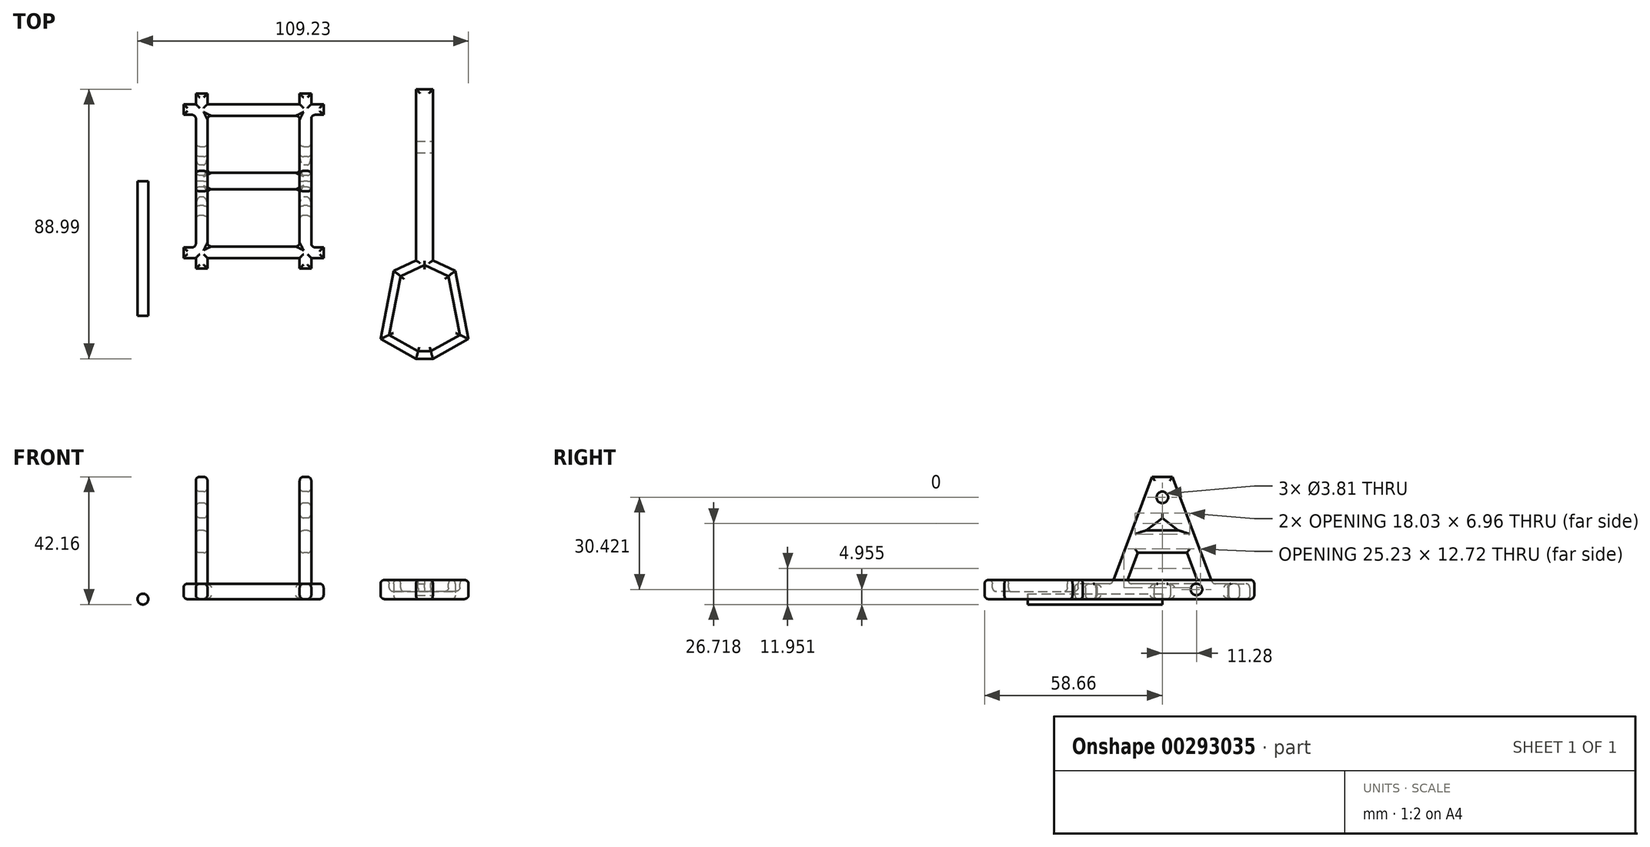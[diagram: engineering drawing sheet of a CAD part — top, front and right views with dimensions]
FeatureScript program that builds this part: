
annotation { "Feature Type Name" : "Feature", "Feature Type Description" : "" }
export const myFeature = defineFeature(function(context is Context, id is Id, definition is map)
    precondition{}
    {
        {
            var Q0;
            Q0=qCreatedBy(makeId("Top.planeOp"),FACE);
            var sketch = newSketch(context, id + "F0", { "sketchPlane" : qUnion([Q0])});
            skLineSegment(sketch, "E0.bottom", {"start": v(19.05, 25.4) * mm, "end": v(-19.05, 25.4) * mm});
            skLineSegment(sketch, "E0.top", {"start": v(19.05, -25.4) * mm, "end": v(-19.05, -25.4) * mm});
            skLineSegment(sketch, "E0.left", {"start": v(19.05, 21.89) * mm, "end": v(19.05, -21.89) * mm});
            skLineSegment(sketch, "E0.right", {"start": v(-19.05, 21.89) * mm, "end": v(-19.05, -21.89) * mm});
            skPoint(sketch, "E0.middle", {"position": v(0, 0) * mm});
            skLineSegment(sketch, "E1", {"start": v(-19.05, 25.4) * mm, "end": v(-23.1, 25.4) * mm});
            skLineSegment(sketch, "E2", {"start": v(-23.1, 25.4) * mm, "end": v(-23.1, 21.89) * mm});
            skLineSegment(sketch, "E3", {"start": v(-23.1, 21.89) * mm, "end": v(-19.05, 21.89) * mm});
            skLineSegment(sketch, "E4.MirrorCS", {"start": v(-23.1, -25.4) * mm, "end": v(-23.1, -21.89) * mm});
            skLineSegment(sketch, "E5.MirrorCS", {"start": v(-19.05, -25.4) * mm, "end": v(-23.1, -25.4) * mm});
            skLineSegment(sketch, "E6.MirrorCS", {"start": v(-23.1, -21.89) * mm, "end": v(-19.05, -21.89) * mm});
            skLineSegment(sketch, "E7.MirrorCS", {"start": v(23.1, 21.89) * mm, "end": v(19.05, 21.89) * mm});
            skLineSegment(sketch, "E8.MirrorCS", {"start": v(23.1, 25.4) * mm, "end": v(23.1, 21.89) * mm});
            skLineSegment(sketch, "E9.MirrorCS", {"start": v(19.05, 25.4) * mm, "end": v(23.1, 25.4) * mm});
            skLineSegment(sketch, "E10.MirrorCS", {"start": v(23.1, -21.89) * mm, "end": v(19.05, -21.89) * mm});
            skLineSegment(sketch, "E11.MirrorCS", {"start": v(23.1, -25.4) * mm, "end": v(23.1, -21.89) * mm});
            skLineSegment(sketch, "E12.MirrorCS", {"start": v(19.05, -25.4) * mm, "end": v(23.1, -25.4) * mm});
            skLineSegment(sketch, "E13.bottom", {"start": v(-15.23, 21.58) * mm, "end": v(15.23, 21.58) * mm});
            skLineSegment(sketch, "E13.top", {"start": v(-15.23, -21.58) * mm, "end": v(15.23, -21.58) * mm});
            skLineSegment(sketch, "E13.left", {"start": v(-15.23, 21.58) * mm, "end": v(-15.23, 2.71) * mm});
            skLineSegment(sketch, "E13.right", {"start": v(15.23, 21.58) * mm, "end": v(15.23, 2.71) * mm});
            skLineSegment(sketch, "E14", {"start": v(-15.23, 2.71) * mm, "end": v(15.23, 2.71) * mm});
            skPoint(sketch, "E15.endSnap0", {"position": v(-15.23, 0) * mm});
            skLineSegment(sketch, "E16.MirrorCS", {"start": v(-15.23, -2.71) * mm, "end": v(15.23, -2.71) * mm});
            skLineSegment(sketch, "E17.trimOffspring", {"start": v(-15.23, -2.71) * mm, "end": v(-15.23, -21.58) * mm});
            skLineSegment(sketch, "E18.trimOffspring", {"start": v(15.23, -2.71) * mm, "end": v(15.23, -21.58) * mm});
            skLineSegment(sketch, "E19", {"start": v(-19.05, -25.4) * mm, "end": v(-19.05, -28.88) * mm});
            skLineSegment(sketch, "E20", {"start": v(-19.05, -28.88) * mm, "end": v(-15.23, -28.88) * mm});
            skLineSegment(sketch, "E21", {"start": v(-15.23, -28.88) * mm, "end": v(-15.23, -25.4) * mm});
            skPoint(sketch, "E22.endSnap0", {"position": v(0, -2.71) * mm});
            skLineSegment(sketch, "E23.MirrorCS", {"start": v(19.05, -28.88) * mm, "end": v(15.23, -28.88) * mm});
            skLineSegment(sketch, "E24.MirrorCS", {"start": v(19.05, -25.4) * mm, "end": v(19.05, -28.88) * mm});
            skLineSegment(sketch, "E25.MirrorCS", {"start": v(15.23, -28.88) * mm, "end": v(15.23, -25.4) * mm});
            skLineSegment(sketch, "E26.MirrorCS", {"start": v(-19.05, 25.4) * mm, "end": v(-19.05, 28.88) * mm});
            skLineSegment(sketch, "E27.MirrorCS", {"start": v(-19.05, 28.88) * mm, "end": v(-15.23, 28.88) * mm});
            skLineSegment(sketch, "E28.MirrorCS", {"start": v(-15.23, 28.88) * mm, "end": v(-15.23, 25.4) * mm});
            skLineSegment(sketch, "E29.MirrorCS", {"start": v(15.23, 28.88) * mm, "end": v(15.23, 25.4) * mm});
            skLineSegment(sketch, "E30.MirrorCS", {"start": v(19.05, 28.88) * mm, "end": v(15.23, 28.88) * mm});
            skLineSegment(sketch, "E31.MirrorCS", {"start": v(19.05, 25.4) * mm, "end": v(19.05, 28.88) * mm});
            skPoint(sketch, "E32.orphan", {"position": v(0, -8.45) * mm});
            skSolve(sketch);
        }
        {
            var Q0;
            Q0 = qSketchRegion(id + "F0", true);
            extrude(context, id + "F1", {"entities" : qUnion([Q0]), "depth" : 5.08 * mm});
        }
        {
            var Q0;
            Q0=qCreatedBy(makeId("Right.planeOp"),FACE);
            var sketch = newSketch(context, id + "F2", { "sketchPlane" : qUnion([Q0])});
            skLineSegment(sketch, "E33.0.0", {"start": v(21.89, 0) * mm, "end": v(-21.89, 0) * mm});
            skLineSegment(sketch, "E33.0.1", {"start": v(-21.89, 0) * mm, "end": v(-21.89, 5.08) * mm});
            skLineSegment(sketch, "E33.0.2", {"start": v(-21.89, 5.08) * mm, "end": v(21.89, 5.08) * mm});
            skLineSegment(sketch, "E33.0.3", {"start": v(21.89, 5.08) * mm, "end": v(21.89, 0) * mm});
            skLineSegment(sketch, "E34", {"start": v(16.63, 5.08) * mm, "end": v(3.36, 40.38) * mm});
            skLineSegment(sketch, "E35.MirrorCS", {"start": v(-16.63, 5.08) * mm, "end": v(-3.36, 40.38) * mm});
            skLineSegment(sketch, "E36", {"start": v(3.36, 40.38) * mm, "end": v(-3.36, 40.38) * mm});
            skLineSegment(sketch, "E37", {"start": v(11.93, 5.08) * mm, "end": v(8.1, 15.26) * mm});
            skLineSegment(sketch, "E38", {"start": v(0, 0) * mm, "end": v(0, 15.33) * mm});
            skLineSegment(sketch, "E39.MirrorCS", {"start": v(-11.93, 5.08) * mm, "end": v(-8.1, 15.26) * mm});
            skPoint(sketch, "E40.orphan", {"position": v(-0.73, 38.74) * mm});
            skPoint(sketch, "E41.orphan", {"position": v(0.73, 38.74) * mm});
            skLineSegment(sketch, "E42", {"start": v(5.29, 22.73) * mm, "end": v(-5.29, 22.73) * mm});
            skLineSegment(sketch, "E43", {"start": v(8.1, 15.26) * mm, "end": v(-8.1, 15.26) * mm});
            skPoint(sketch, "E44.orphan", {"position": v(-10, 22.73) * mm});
            skPoint(sketch, "E45.orphan", {"position": v(10, 22.73) * mm});
            skLineSegment(sketch, "E46", {"start": v(5.29, 22.73) * mm, "end": v(0, 26.81) * mm});
            skLineSegment(sketch, "E47", {"start": v(0, 26.81) * mm, "end": v(-5.29, 22.73) * mm});
            skLineSegment(sketch, "E48", {"start": v(0, 40.38) * mm, "end": v(0, 26.81) * mm});
            skCircle(sketch, "E49", {"center": v(0, 33.6) * mm, "radius": 1.9 * mm});
            skSolve(sketch);
        }
        {
            var Q0;
            {var subQ6=sQuery(id+"F2.wireOp",EDGE,"E34");Q0=makeQuery(id+"F2.imprint","IMPRINT",FACE,{"disambiguationData":[TD([[makeQuery(id+"F2.imprint","IMPRINT",EDGE,{"derivedFrom":subQ6}),1.0]])]});}
            extrude(context, id + "F3", {"entities" : qUnion([Q0]), "operationType" : NewBodyOperationType.ADD, "depth" : 19.05 * mm, "hasSecondDirection" : true, "secondDirectionOppositeDirection" : true, "secondDirectionDepth" : 19.05 * mm});
        }
        {
            var Q0;
            Q0=makeQuery(id+"F3.opExtrude","SWEPT_FACE",FACE,{"disambiguationData":[OSD([sQuery(id+"F2.wireOp",EDGE,"E36")])]});
            var sketch = newSketch(context, id + "F4", { "sketchPlane" : qUnion([Q0])});
            skLineSegment(sketch, "E50.0.0", {"start": v(-19.05, 16.63) * mm, "end": v(-19.05, 3.36) * mm});
            skLineSegment(sketch, "E50.0.1", {"start": v(-19.05, 3.36) * mm, "end": v(19.05, 3.36) * mm});
            skLineSegment(sketch, "E50.0.2", {"start": v(19.05, 3.36) * mm, "end": v(19.05, 16.63) * mm});
            skLineSegment(sketch, "E50.0.3", {"start": v(19.05, 16.63) * mm, "end": v(15.23, 16.63) * mm});
            skLineSegment(sketch, "E50.0.4", {"start": v(15.23, 16.63) * mm, "end": v(-15.23, 16.63) * mm});
            skLineSegment(sketch, "E50.0.5", {"start": v(-15.23, 16.63) * mm, "end": v(-19.05, 16.63) * mm});
            skLineSegment(sketch, "E51.0.0", {"start": v(-19.05, -3.36) * mm, "end": v(-19.05, -16.63) * mm});
            skLineSegment(sketch, "E51.0.1", {"start": v(-19.05, -16.63) * mm, "end": v(-15.23, -16.63) * mm});
            skLineSegment(sketch, "E51.0.2", {"start": v(-15.23, -16.63) * mm, "end": v(15.23, -16.63) * mm});
            skLineSegment(sketch, "E51.0.3", {"start": v(15.23, -16.63) * mm, "end": v(19.05, -16.63) * mm});
            skLineSegment(sketch, "E51.0.4", {"start": v(19.05, -16.63) * mm, "end": v(19.05, -3.36) * mm});
            skLineSegment(sketch, "E51.0.5", {"start": v(19.05, -3.36) * mm, "end": v(-19.05, -3.36) * mm});
            skLineSegment(sketch, "E52.0.0", {"start": v(19.05, -21.89) * mm, "end": v(19.05, -16.63) * mm});
            skLineSegment(sketch, "E52.0.1", {"start": v(19.05, -16.63) * mm, "end": v(15.23, -16.63) * mm});
            skLineSegment(sketch, "E52.0.2", {"start": v(15.23, -16.63) * mm, "end": v(15.23, -21.58) * mm});
            skLineSegment(sketch, "E52.0.3", {"start": v(15.23, -21.58) * mm, "end": v(-15.23, -21.58) * mm});
            skLineSegment(sketch, "E52.0.4", {"start": v(-15.23, -21.58) * mm, "end": v(-15.23, -16.63) * mm});
            skLineSegment(sketch, "E52.0.5", {"start": v(-15.23, -16.63) * mm, "end": v(-19.05, -16.63) * mm});
            skLineSegment(sketch, "E52.0.6", {"start": v(-19.05, -16.63) * mm, "end": v(-19.05, -21.89) * mm});
            skLineSegment(sketch, "E52.0.7", {"start": v(-19.05, -21.89) * mm, "end": v(-23.1, -21.89) * mm});
            skLineSegment(sketch, "E52.0.8", {"start": v(-23.1, -21.89) * mm, "end": v(-23.1, -25.4) * mm});
            skLineSegment(sketch, "E52.0.9", {"start": v(-23.1, -25.4) * mm, "end": v(-19.05, -25.4) * mm});
            skLineSegment(sketch, "E52.0.10", {"start": v(-19.05, -25.4) * mm, "end": v(-19.05, -28.88) * mm});
            skLineSegment(sketch, "E52.0.11", {"start": v(-19.05, -28.88) * mm, "end": v(-15.23, -28.88) * mm});
            skLineSegment(sketch, "E52.0.12", {"start": v(-15.23, -28.88) * mm, "end": v(-15.23, -25.4) * mm});
            skLineSegment(sketch, "E52.0.13", {"start": v(-15.23, -25.4) * mm, "end": v(15.23, -25.4) * mm});
            skLineSegment(sketch, "E52.0.14", {"start": v(15.23, -25.4) * mm, "end": v(15.23, -28.88) * mm});
            skLineSegment(sketch, "E52.0.15", {"start": v(15.23, -28.88) * mm, "end": v(19.05, -28.88) * mm});
            skLineSegment(sketch, "E52.0.16", {"start": v(19.05, -28.88) * mm, "end": v(19.05, -25.4) * mm});
            skLineSegment(sketch, "E52.0.17", {"start": v(19.05, -25.4) * mm, "end": v(23.1, -25.4) * mm});
            skLineSegment(sketch, "E52.0.18", {"start": v(23.1, -25.4) * mm, "end": v(23.1, -21.89) * mm});
            skLineSegment(sketch, "E52.0.19", {"start": v(23.1, -21.89) * mm, "end": v(19.05, -21.89) * mm});
            skLineSegment(sketch, "E53", {"start": v(-15.23, -16.63) * mm, "end": v(-15.23, 16.63) * mm});
            skLineSegment(sketch, "E54", {"start": v(15.23, 16.63) * mm, "end": v(15.23, -16.63) * mm});
            skSolve(sketch);
        }
        {
            var Q0;
            {var subQ5=sQuery(id+"F4.wireOp",EDGE,"E50.0.4");Q0=makeQuery(id+"F4.imprint","IMPRINT",FACE,{"disambiguationData":[TD([[makeQuery(id+"F4.imprint","IMPRINT",EDGE,{"derivedFrom":subQ5}),1.0]])]});}
            var Q1;
            {var subQ0=sQuery(id+"F4.wireOp",EDGE,"E54");var subQ1=sQuery(id+"F4.wireOp",EDGE,"E50.0.1");var subQ2=makeQuery(id+"F4.imprint","INTERSECT",VERTEX,{"derivedFrom":[subQ1,subQ0]});Q1=makeQuery(id+"F4.imprint","IMPRINT",FACE,{"disambiguationData":[TD([[makeQuery(id+"F4.imprint","IMPRINT",EDGE,{"disambiguationData":[TD([[subQ2,-1.0]])],"derivedFrom":subQ1}),1.0]])]});}
            var Q2;
            {var subQ0=sQuery(id+"F4.wireOp",EDGE,"E51.0.2");Q2=makeQuery(id+"F4.imprint","IMPRINT",FACE,{"disambiguationData":[TD([[makeQuery(id+"F4.imprint","IMPRINT",EDGE,{"derivedFrom":subQ0}),1.0]])]});}
            var Q3;
            {var subQ0=sQuery(id+"F0.wireOp",EDGE,"E18.trimOffspring");var subQ11=sQuery(id+"F0.wireOp",EDGE,"E0.right");var subQ12=sQuery(id+"F0.wireOp",EDGE,"E17.trimOffspring");var subQ13=sQuery(id+"F0.wireOp",EDGE,"E0.left");var subQ14=sQuery(id+"F0.wireOp",EDGE,"E16.MirrorCS");var subQ15=sQuery(id+"F0.wireOp",EDGE,"E14");var subQ16=sQuery(id+"F0.wireOp",EDGE,"E13.left");var subQ17=sQuery(id+"F0.wireOp",EDGE,"E13.right");Q3=makeQuery(id+"F3.boolean.opBoolean","SPLIT",FACE,{"disambiguationData":[TD([makeQuery(id+"F1.opExtrude","SWEPT_FACE",FACE,{"disambiguationData":[OSD([subQ15])]})])],"derivedFrom":makeQuery(id+"F1.opExtrude","CAP_FACE",FACE,{"disambiguationData":[OSD([sQuery(id+"F0.wireOp",EDGE,"E0.bottom"),sQuery(id+"F0.wireOp",EDGE,"E0.top"),subQ13,subQ11,sQuery(id+"F0.wireOp",EDGE,"E1"),sQuery(id+"F0.wireOp",EDGE,"E2"),sQuery(id+"F0.wireOp",EDGE,"E3"),sQuery(id+"F0.wireOp",EDGE,"E4.MirrorCS"),sQuery(id+"F0.wireOp",EDGE,"E5.MirrorCS"),sQuery(id+"F0.wireOp",EDGE,"E6.MirrorCS"),sQuery(id+"F0.wireOp",EDGE,"E7.MirrorCS"),sQuery(id+"F0.wireOp",EDGE,"E8.MirrorCS"),sQuery(id+"F0.wireOp",EDGE,"E9.MirrorCS"),sQuery(id+"F0.wireOp",EDGE,"E10.MirrorCS"),sQuery(id+"F0.wireOp",EDGE,"E11.MirrorCS"),sQuery(id+"F0.wireOp",EDGE,"E12.MirrorCS"),sQuery(id+"F0.wireOp",EDGE,"E13.bottom"),sQuery(id+"F0.wireOp",EDGE,"E13.top"),subQ16,subQ17,subQ15,subQ14,subQ12,subQ0,sQuery(id+"F0.wireOp",EDGE,"E19"),sQuery(id+"F0.wireOp",EDGE,"E20"),sQuery(id+"F0.wireOp",EDGE,"E21"),sQuery(id+"F0.wireOp",EDGE,"E23.MirrorCS"),sQuery(id+"F0.wireOp",EDGE,"E24.MirrorCS"),sQuery(id+"F0.wireOp",EDGE,"E25.MirrorCS"),sQuery(id+"F0.wireOp",EDGE,"E26.MirrorCS"),sQuery(id+"F0.wireOp",EDGE,"E27.MirrorCS"),sQuery(id+"F0.wireOp",EDGE,"E28.MirrorCS"),sQuery(id+"F0.wireOp",EDGE,"E29.MirrorCS"),sQuery(id+"F0.wireOp",EDGE,"E30.MirrorCS"),sQuery(id+"F0.wireOp",EDGE,"E31.MirrorCS")])],"isStart":false})});}
            extrude(context, id + "F5", {"entities" : qUnion([Q0, Q1, Q2]), "operationType" : NewBodyOperationType.REMOVE, "endBound" : BoundingType.UP_TO_SURFACE, "oppositeDirection" : true, "endBoundEntityFace" : qUnion([Q3]), "depth" : 25.4 * mm});
        }
        {
            var Q0;
            Q0=qCreatedBy(makeId("Top.planeOp"),FACE);
            var sketch = newSketch(context, id + "F6", { "sketchPlane" : qUnion([Q0])});
            skLineSegment(sketch, "E55", {"start": v(59.18, 0) * mm, "end": v(59.18, 30.33) * mm});
            skLineSegment(sketch, "E56", {"start": v(59.18, 30.33) * mm, "end": v(53.67, 30.33) * mm});
            skLineSegment(sketch, "E57", {"start": v(53.67, 30.33) * mm, "end": v(53.67, -26.25) * mm});
            skLineSegment(sketch, "E58", {"start": v(53.67, -26.25) * mm, "end": v(46.26, -29.62) * mm});
            skLineSegment(sketch, "E59", {"start": v(46.26, -29.62) * mm, "end": v(41.91, -52.14) * mm});
            skLineSegment(sketch, "E60", {"start": v(41.91, -52.14) * mm, "end": v(53.67, -58.66) * mm});
            skLineSegment(sketch, "E61", {"start": v(53.67, -58.66) * mm, "end": v(56.42, -58.66) * mm});
            skPoint(sketch, "E61.endSnap0", {"position": v(56.42, 30.33) * mm});
            skLineSegment(sketch, "E62", {"start": v(56.42, -58.66) * mm, "end": v(56.42, -51.22) * mm});
            skLineSegment(sketch, "E63.MirrorCS", {"start": v(59.18, -58.66) * mm, "end": v(56.42, -58.66) * mm});
            skLineSegment(sketch, "E64.MirrorCS", {"start": v(70.94, -52.14) * mm, "end": v(59.18, -58.66) * mm});
            skLineSegment(sketch, "E65.MirrorCS", {"start": v(66.6, -29.62) * mm, "end": v(70.94, -52.14) * mm});
            skLineSegment(sketch, "E66.MirrorCS", {"start": v(59.18, -26.25) * mm, "end": v(66.6, -29.62) * mm});
            skLineSegment(sketch, "E67.MirrorCS", {"start": v(59.18, 30.33) * mm, "end": v(59.18, -26.25) * mm});
            skSolve(sketch);
        }
        {
            var Q0;
            Q0 = qSketchRegion(id + "F6", true);
            extrude(context, id + "F7", {"entities" : qUnion([Q0]), "depth" : 6.35 * mm});
        }
        {
            var Q0;
            Q0=makeQuery(id+"F7.opExtrude","CAP_FACE",FACE,{"disambiguationData":[OSD([sQuery(id+"F6.wireOp",EDGE,"E56"),sQuery(id+"F6.wireOp",EDGE,"E57"),sQuery(id+"F6.wireOp",EDGE,"E58"),sQuery(id+"F6.wireOp",EDGE,"E59"),sQuery(id+"F6.wireOp",EDGE,"E60"),sQuery(id+"F6.wireOp",EDGE,"E61"),sQuery(id+"F6.wireOp",EDGE,"E63.MirrorCS"),sQuery(id+"F6.wireOp",EDGE,"E64.MirrorCS"),sQuery(id+"F6.wireOp",EDGE,"E65.MirrorCS"),sQuery(id+"F6.wireOp",EDGE,"E66.MirrorCS"),sQuery(id+"F6.wireOp",EDGE,"E67.MirrorCS")])],"isStart":false});
            var sketch = newSketch(context, id + "F8", { "sketchPlane" : qUnion([Q0])});
            skLineSegment(sketch, "E68.0", {"start": v(44.75, -50.8) * mm, "end": v(54.33, -56.12) * mm});
            skLineSegment(sketch, "E68.1", {"start": v(48.5, -31.4) * mm, "end": v(44.75, -50.8) * mm});
            skLineSegment(sketch, "E68.2", {"start": v(58.52, -56.12) * mm, "end": v(68.1, -50.8) * mm});
            skLineSegment(sketch, "E68.3", {"start": v(68.1, -50.8) * mm, "end": v(64.35, -31.4) * mm});
            skLineSegment(sketch, "E68.4", {"start": v(64.35, -31.4) * mm, "end": v(56.42, -27.78) * mm});
            skLineSegment(sketch, "E68.5", {"start": v(54.33, -56.12) * mm, "end": v(58.52, -56.12) * mm});
            skLineSegment(sketch, "E68.6", {"start": v(56.42, -27.78) * mm, "end": v(48.5, -31.4) * mm});
            skSolve(sketch);
        }
        {
            var Q0;
            Q0 = qSketchRegion(id + "F8", true);
            extrude(context, id + "F9", {"entities" : qUnion([Q0]), "operationType" : NewBodyOperationType.REMOVE, "oppositeDirection" : true, "depth" : 3.8 * mm});
        }
        {
            var Q0;
            Q0=makeQuery(id+"F7.opExtrude","SWEPT_FACE",FACE,{"disambiguationData":[OSD([sQuery(id+"F6.wireOp",EDGE,"E67.MirrorCS")])]});
            var sketch = newSketch(context, id + "F10", { "sketchPlane" : qUnion([Q0])});
            skLineSegment(sketch, "E69", {"start": v(30.33, 3.18) * mm, "end": v(11.28, 3.18) * mm});
            skCircle(sketch, "E70", {"center": v(11.28, 3.18) * mm, "radius": 1.9 * mm});
            skSolve(sketch);
        }
        {
            var Q0;
            Q0 = qSketchRegion(id + "F10", true);
            extrude(context, id + "F11", {"entities" : qUnion([Q0]), "operationType" : NewBodyOperationType.REMOVE, "oppositeDirection" : true, "depth" : 25.4 * mm});
        }
        {
            var Q0;
            Q0=makeQuery(id+"F9.boolean.opBoolean","COPY",FACE,{"derivedFrom":makeQuery(id+"F9.opExtrude","CAP_FACE",FACE,{"disambiguationData":[OSD([sQuery(id+"F8.wireOp",EDGE,"E68.0"),sQuery(id+"F8.wireOp",EDGE,"E68.1"),sQuery(id+"F8.wireOp",EDGE,"E68.2"),sQuery(id+"F8.wireOp",EDGE,"E68.3"),sQuery(id+"F8.wireOp",EDGE,"E68.4"),sQuery(id+"F8.wireOp",EDGE,"E68.5"),sQuery(id+"F8.wireOp",EDGE,"E68.6")])],"isStart":false})});
            var Q1;
            Q1=makeQuery(id+"F9.boolean.opBoolean","COPY",EDGE,{"derivedFrom":makeQuery(id+"F9.opExtrude","CAP_EDGE",EDGE,{"disambiguationData":[OSD([sQuery(id+"F8.wireOp",EDGE,"E68.0")])],"isStart":true})});
            var Q2;
            Q2=makeQuery(id+"F7.opExtrude","CAP_FACE",FACE,{"disambiguationData":[OSD([sQuery(id+"F6.wireOp",EDGE,"E56"),sQuery(id+"F6.wireOp",EDGE,"E57"),sQuery(id+"F6.wireOp",EDGE,"E58"),sQuery(id+"F6.wireOp",EDGE,"E59"),sQuery(id+"F6.wireOp",EDGE,"E60"),sQuery(id+"F6.wireOp",EDGE,"E61"),sQuery(id+"F6.wireOp",EDGE,"E63.MirrorCS"),sQuery(id+"F6.wireOp",EDGE,"E64.MirrorCS"),sQuery(id+"F6.wireOp",EDGE,"E65.MirrorCS"),sQuery(id+"F6.wireOp",EDGE,"E66.MirrorCS"),sQuery(id+"F6.wireOp",EDGE,"E67.MirrorCS")])],"isStart":false});
            var Q3;
            Q3=makeQuery(id+"F7.opExtrude","CAP_FACE",FACE,{"disambiguationData":[OSD([sQuery(id+"F6.wireOp",EDGE,"E56"),sQuery(id+"F6.wireOp",EDGE,"E57"),sQuery(id+"F6.wireOp",EDGE,"E58"),sQuery(id+"F6.wireOp",EDGE,"E59"),sQuery(id+"F6.wireOp",EDGE,"E60"),sQuery(id+"F6.wireOp",EDGE,"E61"),sQuery(id+"F6.wireOp",EDGE,"E63.MirrorCS"),sQuery(id+"F6.wireOp",EDGE,"E64.MirrorCS"),sQuery(id+"F6.wireOp",EDGE,"E65.MirrorCS"),sQuery(id+"F6.wireOp",EDGE,"E66.MirrorCS"),sQuery(id+"F6.wireOp",EDGE,"E67.MirrorCS")])],"isStart":true});
            fillet(context, id + "F12", {"entities" : qUnion([Q0, Q1, Q2, Q3]), "radius" : 1.27 * mm, "tangentPropagation" : true, "allowEdgeOverflow" : false});
        }
        {
            var Q0;
            Q0=makeQuery(id+"F3.boolean.opBoolean","MERGE",FACE,{"derivedFrom":[makeQuery(id+"F1.opExtrude","SWEPT_FACE",FACE,{"disambiguationData":[OSD([sQuery(id+"F0.wireOp",EDGE,"E0.left")])]}),makeQuery(id+"F3.opExtrude","CAP_FACE",FACE,{"disambiguationData":[OSD([sQuery(id+"F2.wireOp",EDGE,"E33.0.2"),sQuery(id+"F2.wireOp",EDGE,"E34"),sQuery(id+"F2.wireOp",EDGE,"E35.MirrorCS"),sQuery(id+"F2.wireOp",EDGE,"E36"),sQuery(id+"F2.wireOp",EDGE,"E37"),sQuery(id+"F2.wireOp",EDGE,"E39.MirrorCS"),sQuery(id+"F2.wireOp",EDGE,"E42"),sQuery(id+"F2.wireOp",EDGE,"E43"),sQuery(id+"F2.wireOp",EDGE,"E46"),sQuery(id+"F2.wireOp",EDGE,"E47"),sQuery(id+"F2.wireOp",EDGE,"E49")])],"isStart":false})]});
            var Q1;
            Q1=makeQuery(id+"F3.boolean.opBoolean","MERGE",FACE,{"derivedFrom":[makeQuery(id+"F1.opExtrude","SWEPT_FACE",FACE,{"disambiguationData":[OSD([sQuery(id+"F0.wireOp",EDGE,"E0.right")])]}),makeQuery(id+"F3.opExtrude","CAP_FACE",FACE,{"disambiguationData":[OSD([sQuery(id+"F2.wireOp",EDGE,"E33.0.2"),sQuery(id+"F2.wireOp",EDGE,"E34"),sQuery(id+"F2.wireOp",EDGE,"E35.MirrorCS"),sQuery(id+"F2.wireOp",EDGE,"E36"),sQuery(id+"F2.wireOp",EDGE,"E37"),sQuery(id+"F2.wireOp",EDGE,"E39.MirrorCS"),sQuery(id+"F2.wireOp",EDGE,"E42"),sQuery(id+"F2.wireOp",EDGE,"E43"),sQuery(id+"F2.wireOp",EDGE,"E46"),sQuery(id+"F2.wireOp",EDGE,"E47"),sQuery(id+"F2.wireOp",EDGE,"E49")])],"isStart":true})]});
            var Q2;
            {var subQ0=sQuery(id+"F0.wireOp",EDGE,"E9.MirrorCS");var subQ1=sQuery(id+"F0.wireOp",EDGE,"E31.MirrorCS");var subQ2=sQuery(id+"F0.wireOp",EDGE,"E8.MirrorCS");var subQ3=sQuery(id+"F0.wireOp",EDGE,"E30.MirrorCS");var subQ4=sQuery(id+"F0.wireOp",EDGE,"E7.MirrorCS");var subQ5=sQuery(id+"F0.wireOp",EDGE,"E29.MirrorCS");var subQ6=sQuery(id+"F0.wireOp",EDGE,"E3");var subQ8=sQuery(id+"F0.wireOp",EDGE,"E13.bottom");var subQ9=sQuery(id+"F0.wireOp",EDGE,"E2");var subQ12=sQuery(id+"F0.wireOp",EDGE,"E0.bottom");var subQ13=sQuery(id+"F0.wireOp",EDGE,"E0.right");var subQ22=sQuery(id+"F0.wireOp",EDGE,"E0.left");var subQ23=sQuery(id+"F0.wireOp",EDGE,"E1");var subQ24=sQuery(id+"F0.wireOp",EDGE,"E13.left");var subQ25=sQuery(id+"F0.wireOp",EDGE,"E13.right");var subQ26=sQuery(id+"F0.wireOp",EDGE,"E26.MirrorCS");var subQ27=sQuery(id+"F0.wireOp",EDGE,"E27.MirrorCS");var subQ28=sQuery(id+"F0.wireOp",EDGE,"E28.MirrorCS");Q2=makeQuery(id+"F3.boolean.opBoolean","SPLIT",FACE,{"disambiguationData":[TD([makeQuery(id+"F1.opExtrude","SWEPT_FACE",FACE,{"disambiguationData":[OSD([subQ12])]})])],"derivedFrom":makeQuery(id+"F1.opExtrude","CAP_FACE",FACE,{"disambiguationData":[OSD([subQ12,sQuery(id+"F0.wireOp",EDGE,"E0.top"),subQ22,subQ13,subQ23,subQ9,subQ6,sQuery(id+"F0.wireOp",EDGE,"E4.MirrorCS"),sQuery(id+"F0.wireOp",EDGE,"E5.MirrorCS"),sQuery(id+"F0.wireOp",EDGE,"E6.MirrorCS"),subQ4,subQ2,subQ0,sQuery(id+"F0.wireOp",EDGE,"E10.MirrorCS"),sQuery(id+"F0.wireOp",EDGE,"E11.MirrorCS"),sQuery(id+"F0.wireOp",EDGE,"E12.MirrorCS"),subQ8,sQuery(id+"F0.wireOp",EDGE,"E13.top"),subQ24,subQ25,sQuery(id+"F0.wireOp",EDGE,"E14"),sQuery(id+"F0.wireOp",EDGE,"E16.MirrorCS"),sQuery(id+"F0.wireOp",EDGE,"E17.trimOffspring"),sQuery(id+"F0.wireOp",EDGE,"E18.trimOffspring"),sQuery(id+"F0.wireOp",EDGE,"E19"),sQuery(id+"F0.wireOp",EDGE,"E20"),sQuery(id+"F0.wireOp",EDGE,"E21"),sQuery(id+"F0.wireOp",EDGE,"E23.MirrorCS"),sQuery(id+"F0.wireOp",EDGE,"E24.MirrorCS"),sQuery(id+"F0.wireOp",EDGE,"E25.MirrorCS"),subQ26,subQ27,subQ28,subQ5,subQ3,subQ1])],"isStart":false})});}
            var Q3;
            {var subQ0=sQuery(id+"F0.wireOp",EDGE,"E18.trimOffspring");var subQ12=sQuery(id+"F0.wireOp",EDGE,"E0.right");var subQ13=sQuery(id+"F0.wireOp",EDGE,"E17.trimOffspring");var subQ14=sQuery(id+"F0.wireOp",EDGE,"E0.left");var subQ15=sQuery(id+"F0.wireOp",EDGE,"E16.MirrorCS");var subQ16=sQuery(id+"F0.wireOp",EDGE,"E14");var subQ17=sQuery(id+"F0.wireOp",EDGE,"E13.left");var subQ18=sQuery(id+"F0.wireOp",EDGE,"E13.right");Q3=makeQuery(id+"F3.boolean.opBoolean","SPLIT",FACE,{"disambiguationData":[TD([makeQuery(id+"F1.opExtrude","SWEPT_FACE",FACE,{"disambiguationData":[OSD([subQ16])]})])],"derivedFrom":makeQuery(id+"F1.opExtrude","CAP_FACE",FACE,{"disambiguationData":[OSD([sQuery(id+"F0.wireOp",EDGE,"E0.bottom"),sQuery(id+"F0.wireOp",EDGE,"E0.top"),subQ14,subQ12,sQuery(id+"F0.wireOp",EDGE,"E1"),sQuery(id+"F0.wireOp",EDGE,"E2"),sQuery(id+"F0.wireOp",EDGE,"E3"),sQuery(id+"F0.wireOp",EDGE,"E4.MirrorCS"),sQuery(id+"F0.wireOp",EDGE,"E5.MirrorCS"),sQuery(id+"F0.wireOp",EDGE,"E6.MirrorCS"),sQuery(id+"F0.wireOp",EDGE,"E7.MirrorCS"),sQuery(id+"F0.wireOp",EDGE,"E8.MirrorCS"),sQuery(id+"F0.wireOp",EDGE,"E9.MirrorCS"),sQuery(id+"F0.wireOp",EDGE,"E10.MirrorCS"),sQuery(id+"F0.wireOp",EDGE,"E11.MirrorCS"),sQuery(id+"F0.wireOp",EDGE,"E12.MirrorCS"),sQuery(id+"F0.wireOp",EDGE,"E13.bottom"),sQuery(id+"F0.wireOp",EDGE,"E13.top"),subQ17,subQ18,subQ16,subQ15,subQ13,subQ0,sQuery(id+"F0.wireOp",EDGE,"E19"),sQuery(id+"F0.wireOp",EDGE,"E20"),sQuery(id+"F0.wireOp",EDGE,"E21"),sQuery(id+"F0.wireOp",EDGE,"E23.MirrorCS"),sQuery(id+"F0.wireOp",EDGE,"E24.MirrorCS"),sQuery(id+"F0.wireOp",EDGE,"E25.MirrorCS"),sQuery(id+"F0.wireOp",EDGE,"E26.MirrorCS"),sQuery(id+"F0.wireOp",EDGE,"E27.MirrorCS"),sQuery(id+"F0.wireOp",EDGE,"E28.MirrorCS"),sQuery(id+"F0.wireOp",EDGE,"E29.MirrorCS"),sQuery(id+"F0.wireOp",EDGE,"E30.MirrorCS"),sQuery(id+"F0.wireOp",EDGE,"E31.MirrorCS")])],"isStart":false})});}
            var Q4;
            {var subQ0=sQuery(id+"F0.wireOp",EDGE,"E13.top");var subQ1=sQuery(id+"F0.wireOp",EDGE,"E12.MirrorCS");var subQ2=sQuery(id+"F0.wireOp",EDGE,"E6.MirrorCS");var subQ3=sQuery(id+"F0.wireOp",EDGE,"E5.MirrorCS");var subQ4=sQuery(id+"F0.wireOp",EDGE,"E0.top");var subQ5=sQuery(id+"F0.wireOp",EDGE,"E19");var subQ6=sQuery(id+"F0.wireOp",EDGE,"E10.MirrorCS");var subQ7=sQuery(id+"F0.wireOp",EDGE,"E0.left");var subQ8=sQuery(id+"F0.wireOp",EDGE,"E20");var subQ12=sQuery(id+"F0.wireOp",EDGE,"E4.MirrorCS");var subQ13=sQuery(id+"F0.wireOp",EDGE,"E11.MirrorCS");var subQ14=sQuery(id+"F0.wireOp",EDGE,"E0.right");var subQ15=sQuery(id+"F0.wireOp",EDGE,"E21");var subQ24=sQuery(id+"F0.wireOp",EDGE,"E17.trimOffspring");var subQ25=sQuery(id+"F0.wireOp",EDGE,"E18.trimOffspring");var subQ26=sQuery(id+"F0.wireOp",EDGE,"E23.MirrorCS");var subQ27=sQuery(id+"F0.wireOp",EDGE,"E24.MirrorCS");var subQ28=sQuery(id+"F0.wireOp",EDGE,"E25.MirrorCS");Q4=makeQuery(id+"F3.boolean.opBoolean","SPLIT",FACE,{"disambiguationData":[TD([makeQuery(id+"F1.opExtrude","SWEPT_FACE",FACE,{"disambiguationData":[OSD([subQ4])]})])],"derivedFrom":makeQuery(id+"F1.opExtrude","CAP_FACE",FACE,{"disambiguationData":[OSD([sQuery(id+"F0.wireOp",EDGE,"E0.bottom"),subQ4,subQ7,subQ14,sQuery(id+"F0.wireOp",EDGE,"E1"),sQuery(id+"F0.wireOp",EDGE,"E2"),sQuery(id+"F0.wireOp",EDGE,"E3"),subQ12,subQ3,subQ2,sQuery(id+"F0.wireOp",EDGE,"E7.MirrorCS"),sQuery(id+"F0.wireOp",EDGE,"E8.MirrorCS"),sQuery(id+"F0.wireOp",EDGE,"E9.MirrorCS"),subQ6,subQ13,subQ1,sQuery(id+"F0.wireOp",EDGE,"E13.bottom"),subQ0,sQuery(id+"F0.wireOp",EDGE,"E13.left"),sQuery(id+"F0.wireOp",EDGE,"E13.right"),sQuery(id+"F0.wireOp",EDGE,"E14"),sQuery(id+"F0.wireOp",EDGE,"E16.MirrorCS"),subQ24,subQ25,subQ5,subQ8,subQ15,subQ26,subQ27,subQ28,sQuery(id+"F0.wireOp",EDGE,"E26.MirrorCS"),sQuery(id+"F0.wireOp",EDGE,"E27.MirrorCS"),sQuery(id+"F0.wireOp",EDGE,"E28.MirrorCS"),sQuery(id+"F0.wireOp",EDGE,"E29.MirrorCS"),sQuery(id+"F0.wireOp",EDGE,"E30.MirrorCS"),sQuery(id+"F0.wireOp",EDGE,"E31.MirrorCS")])],"isStart":false})});}
            var Q5;
            Q5=makeQuery(id+"F1.opExtrude","CAP_FACE",FACE,{"disambiguationData":[OSD([sQuery(id+"F0.wireOp",EDGE,"E0.bottom"),sQuery(id+"F0.wireOp",EDGE,"E0.top"),sQuery(id+"F0.wireOp",EDGE,"E0.left"),sQuery(id+"F0.wireOp",EDGE,"E0.right"),sQuery(id+"F0.wireOp",EDGE,"E1"),sQuery(id+"F0.wireOp",EDGE,"E2"),sQuery(id+"F0.wireOp",EDGE,"E3"),sQuery(id+"F0.wireOp",EDGE,"E4.MirrorCS"),sQuery(id+"F0.wireOp",EDGE,"E5.MirrorCS"),sQuery(id+"F0.wireOp",EDGE,"E6.MirrorCS"),sQuery(id+"F0.wireOp",EDGE,"E7.MirrorCS"),sQuery(id+"F0.wireOp",EDGE,"E8.MirrorCS"),sQuery(id+"F0.wireOp",EDGE,"E9.MirrorCS"),sQuery(id+"F0.wireOp",EDGE,"E10.MirrorCS"),sQuery(id+"F0.wireOp",EDGE,"E11.MirrorCS"),sQuery(id+"F0.wireOp",EDGE,"E12.MirrorCS"),sQuery(id+"F0.wireOp",EDGE,"E13.bottom"),sQuery(id+"F0.wireOp",EDGE,"E13.top"),sQuery(id+"F0.wireOp",EDGE,"E13.left"),sQuery(id+"F0.wireOp",EDGE,"E13.right"),sQuery(id+"F0.wireOp",EDGE,"E14"),sQuery(id+"F0.wireOp",EDGE,"E16.MirrorCS"),sQuery(id+"F0.wireOp",EDGE,"E17.trimOffspring"),sQuery(id+"F0.wireOp",EDGE,"E18.trimOffspring"),sQuery(id+"F0.wireOp",EDGE,"E19"),sQuery(id+"F0.wireOp",EDGE,"E20"),sQuery(id+"F0.wireOp",EDGE,"E21"),sQuery(id+"F0.wireOp",EDGE,"E23.MirrorCS"),sQuery(id+"F0.wireOp",EDGE,"E24.MirrorCS"),sQuery(id+"F0.wireOp",EDGE,"E25.MirrorCS"),sQuery(id+"F0.wireOp",EDGE,"E26.MirrorCS"),sQuery(id+"F0.wireOp",EDGE,"E27.MirrorCS"),sQuery(id+"F0.wireOp",EDGE,"E28.MirrorCS"),sQuery(id+"F0.wireOp",EDGE,"E29.MirrorCS"),sQuery(id+"F0.wireOp",EDGE,"E30.MirrorCS"),sQuery(id+"F0.wireOp",EDGE,"E31.MirrorCS")])],"isStart":true});
            fillet(context, id + "F13", {"entities" : qUnion([Q0, Q1, Q2, Q3, Q4, Q5]), "radius" : 1.27 * mm, "tangentPropagation" : true, "allowEdgeOverflow" : false});
        }
        {
            var Q0;
            Q0=makeQuery(id+"F5.boolean.opBoolean","MERGE",FACE,{"derivedFrom":[makeQuery(id+"F1.opExtrude","SWEPT_FACE",FACE,{"disambiguationData":[OSD([sQuery(id+"F0.wireOp",EDGE,"E13.left")])]}),makeQuery(id+"F1.opExtrude","SWEPT_FACE",FACE,{"disambiguationData":[OSD([sQuery(id+"F0.wireOp",EDGE,"E17.trimOffspring")])]}),makeQuery(id+"F5.opExtrude","SWEPT_FACE",FACE,{"disambiguationData":[OSD([sQuery(id+"F4.wireOp",EDGE,"E53")])]})]});
            var Q1;
            Q1=makeQuery(id+"F5.boolean.opBoolean","MERGE",FACE,{"derivedFrom":[makeQuery(id+"F1.opExtrude","SWEPT_FACE",FACE,{"disambiguationData":[OSD([sQuery(id+"F0.wireOp",EDGE,"E13.right")])]}),makeQuery(id+"F1.opExtrude","SWEPT_FACE",FACE,{"disambiguationData":[OSD([sQuery(id+"F0.wireOp",EDGE,"E18.trimOffspring")])]}),makeQuery(id+"F5.opExtrude","SWEPT_FACE",FACE,{"disambiguationData":[OSD([sQuery(id+"F4.wireOp",EDGE,"E54")])]})]});
            fillet(context, id + "F14", {"entities" : qUnion([Q0, Q1]), "radius" : 1.27 * mm, "tangentPropagation" : true, "allowEdgeOverflow" : false});
        }
        {
            var Q0;
            Q0=qCreatedBy(makeId("Front.planeOp"),FACE);
            var sketch = newSketch(context, id + "F15", { "sketchPlane" : qUnion([Q0])});
            skCircle(sketch, "E71", {"center": v(-36.51, 0) * mm, "radius": 1.78 * mm});
            skSolve(sketch);
        }
        {
            var Q0;
            Q0 = qSketchRegion(id + "F15", true);
            extrude(context, id + "F16", {"entities" : qUnion([Q0]), "depth" : 44.45 * mm});
        }
    });
